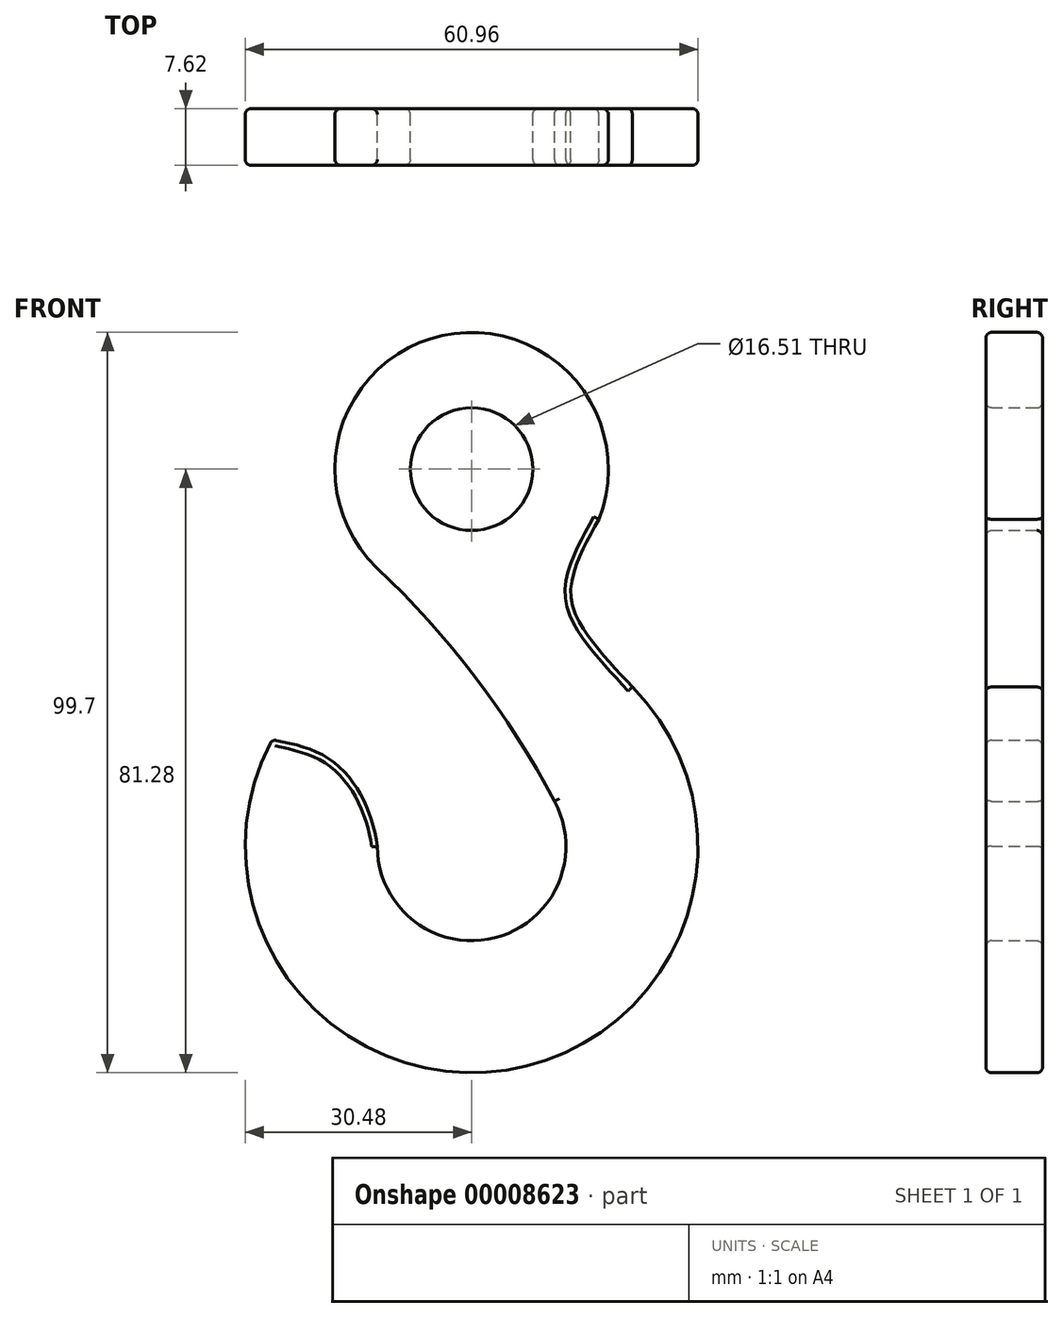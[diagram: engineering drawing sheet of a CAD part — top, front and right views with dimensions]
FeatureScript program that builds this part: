
annotation { "Feature Type Name" : "Feature", "Feature Type Description" : "" }
export const myFeature = defineFeature(function(context is Context, id is Id, definition is map)
    precondition{}
    {
        {
            var Q0;
            Q0=qCreatedBy(makeId("Front.planeOp"),FACE);
            var sketch = newSketch(context, id + "F0", { "sketchPlane" : qUnion([Q0])});
            skArc(sketch, "E0", {"start": v(-12.7, 0) * mm, "mid": v(3.14, -12.3) * mm, "end": v(11.15, 6.08) * mm});
            skArc(sketch, "E1.0", {"start": v(-26.87, 14.38) * mm, "mid": v(4.4, -30.16) * mm, "end": v(21.64, 21.47) * mm});
            skCircle(sketch, "E2", {"center": v(0, 50.8) * mm, "radius": 8.26 * mm});
            skArc(sketch, "E3.0", {"start": v(17.14, 44.06) * mm, "mid": v(-4.08, 68.76) * mm, "end": v(-12.54, 37.32) * mm});
            skFitSpline(sketch, "E4", {"points": [v(17.14, 44.06) * mm, v(21.64, 21.47) * mm], "startDerivative": vector(-17.77, -31.55) * mm, "endDerivative": vector(29.2, -31.2) * mm});
            skArc(sketch, "E5", {"start": v(11.15, 6.08) * mm, "mid": v(0.5, 22.79) * mm, "end": v(-12.76, 37.52) * mm});
            skFitSpline(sketch, "E6", {"points": [v(-12.7, 0) * mm, v(-17.4, 10.3) * mm, v(-26.87, 14.38) * mm], "startDerivative": vector(-3.92, 27.57) * mm, "endDerivative": vector(-30.42, 5.6) * mm});
            skSolve(sketch);
        }
        {
            var Q0;
            {var subQ3=sQuery(id+"F0.wireOp",EDGE,"E0");Q0=makeQuery(id+"F0.imprint","IMPRINT",FACE,{"disambiguationData":[TD([[makeQuery(id+"F0.imprint","IMPRINT",EDGE,{"derivedFrom":subQ3}),-1.0]])]});}
            extrude(context, id + "F1", {"entities" : qUnion([Q0]), "depth" : 7.62 * mm});
        }
        {
            var Q0;
            Q0=makeQuery(id+"F1.opExtrude","CAP_EDGE",EDGE,{"disambiguationData":[OSD([sQuery(id+"F0.wireOp",EDGE,"E5")])],"isStart":false});
            var Q1;
            Q1=makeQuery(id+"F1.opExtrude","CAP_EDGE",EDGE,{"disambiguationData":[OSD([sQuery(id+"F0.wireOp",EDGE,"E6")])],"isStart":false});
            var Q2;
            Q2=makeQuery(id+"F1.opExtrude","CAP_EDGE",EDGE,{"disambiguationData":[OSD([sQuery(id+"F0.wireOp",EDGE,"E1.0")])],"isStart":false});
            var Q3;
            Q3=makeQuery(id+"F1.opExtrude","CAP_EDGE",EDGE,{"disambiguationData":[OSD([sQuery(id+"F0.wireOp",EDGE,"E3.0")])],"isStart":false});
            var Q4;
            Q4=makeQuery(id+"F1.opExtrude","CAP_EDGE",EDGE,{"disambiguationData":[OSD([sQuery(id+"F0.wireOp",EDGE,"E3.0")])],"isStart":true});
            var Q5;
            Q5=makeQuery(id+"F1.opExtrude","CAP_EDGE",EDGE,{"disambiguationData":[OSD([sQuery(id+"F0.wireOp",EDGE,"E1.0")])],"isStart":true});
            var Q6;
            Q6=makeQuery(id+"F1.opExtrude","CAP_EDGE",EDGE,{"disambiguationData":[OSD([sQuery(id+"F0.wireOp",EDGE,"E4")])],"isStart":true});
            var Q7;
            Q7=makeQuery(id+"F1.opExtrude","CAP_EDGE",EDGE,{"disambiguationData":[OSD([sQuery(id+"F0.wireOp",EDGE,"E4")])],"isStart":false});
            var Q8;
            Q8=makeQuery(id+"F1.opExtrude","CAP_EDGE",EDGE,{"disambiguationData":[OSD([sQuery(id+"F0.wireOp",EDGE,"E0")])],"isStart":true});
            var Q9;
            Q9=makeQuery(id+"F1.opExtrude","CAP_EDGE",EDGE,{"disambiguationData":[OSD([sQuery(id+"F0.wireOp",EDGE,"E5")])],"isStart":true});
            var Q10;
            Q10=makeQuery(id+"F1.opExtrude","CAP_EDGE",EDGE,{"disambiguationData":[OSD([sQuery(id+"F0.wireOp",EDGE,"E6")])],"isStart":true});
            var Q11;
            Q11=makeQuery(id+"F1.opExtrude","CAP_EDGE",EDGE,{"disambiguationData":[OSD([sQuery(id+"F0.wireOp",EDGE,"E0")])],"isStart":false});
            var Q12;
            Q12=makeQuery(id+"F1.opExtrude","SWEPT_EDGE",EDGE,{"disambiguationData":[OSD([sQuery(id+"F0.wireOp",EDGE,"E1.0"),sQuery(id+"F0.wireOp",EDGE,"E6")])]});
            var Q13;
            Q13=makeQuery(id+"F1.opExtrude","CAP_EDGE",EDGE,{"disambiguationData":[OSD([sQuery(id+"F0.wireOp",EDGE,"E2")])],"isStart":false});
            var Q14;
            Q14=makeQuery(id+"F1.opExtrude","CAP_EDGE",EDGE,{"disambiguationData":[OSD([sQuery(id+"F0.wireOp",EDGE,"E2")])],"isStart":true});
            fillet(context, id + "F2", {"entities" : qUnion([Q0, Q1, Q2, Q3, Q4, Q5, Q6, Q7, Q8, Q9, Q10, Q11, Q12, Q13, Q14]), "radius" : 0.76 * mm, "tangentPropagation" : true, "allowEdgeOverflow" : false});
        }
    });
